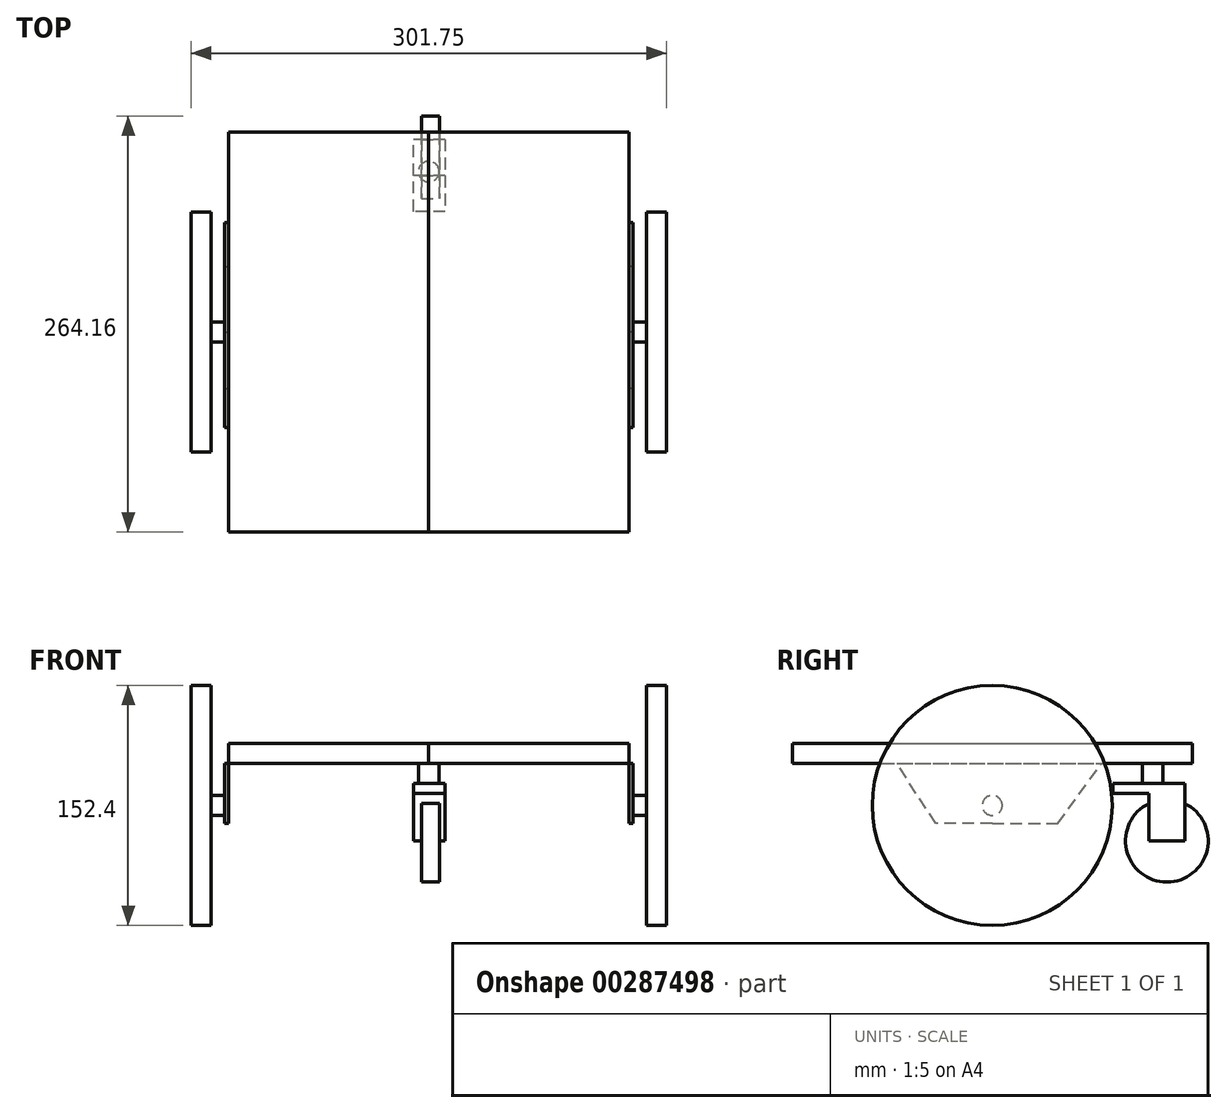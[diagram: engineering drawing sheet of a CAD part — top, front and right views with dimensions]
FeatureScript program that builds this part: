
annotation { "Feature Type Name" : "Feature", "Feature Type Description" : "" }
export const myFeature = defineFeature(function(context is Context, id is Id, definition is map)
    precondition{}
    {
        {
            var Q0;
            Q0=qCreatedBy(makeId("Top.planeOp"),FACE);
            var sketch = newSketch(context, id + "F0", { "sketchPlane" : qUnion([Q0])});
            skLineSegment(sketch, "E0.bottom", {"start": v(-82.1, -91.16) * mm, "end": v(44.9, -91.16) * mm});
            skLineSegment(sketch, "E0.top", {"start": v(-82.1, 162.84) * mm, "end": v(44.9, 162.84) * mm});
            skLineSegment(sketch, "E0.left", {"start": v(-82.1, -91.16) * mm, "end": v(-82.1, 162.84) * mm});
            skLineSegment(sketch, "E0.right", {"start": v(44.9, -91.16) * mm, "end": v(44.9, 162.84) * mm});
            skSolve(sketch);
        }
        {
            var Q0;
            Q0 = qSketchRegion(id + "F0", true);
            extrude(context, id + "F1", {"entities" : qUnion([Q0]), "depth" : 12.7 * mm});
        }
        {
            var Q0;
            Q0=makeQuery(id+"F1.opExtrude","SWEPT_FACE",FACE,{"disambiguationData":[OSD([sQuery(id+"F0.wireOp",EDGE,"E0.left")])]});
            var sketch = newSketch(context, id + "F2", { "sketchPlane" : qUnion([Q0])});
            skLineSegment(sketch, "E1", {"start": v(-35.84, 12.7) * mm, "end": v(-35.84, 0) * mm});
            skLineSegment(sketch, "E2", {"start": v(-35.84, 0) * mm, "end": v(-35.84, -26.62) * mm});
            skCircle(sketch, "E3", {"center": v(-35.84, -26.62) * mm, "radius": 6.35 * mm});
            skSolve(sketch);
        }
        {
            var Q0;
            Q0 = qSketchRegion(id + "F2", true);
            extrude(context, id + "F3", {"entities" : qUnion([Q0]), "depth" : 11.18 * mm});
        }
        {
            var Q0;
            Q0=makeQuery(id+"F3.opExtrude","CAP_FACE",FACE,{"disambiguationData":[OSD([sQuery(id+"F2.wireOp",EDGE,"E3")])],"isStart":false});
            var sketch = newSketch(context, id + "F4", { "sketchPlane" : qUnion([Q0])});
            skCircle(sketch, "E4", {"center": v(-35.84, -26.62) * mm, "radius": 76.2 * mm});
            skSolve(sketch);
        }
        {
            var Q0;
            Q0 = qSketchRegion(id + "F4", true);
            extrude(context, id + "F5", {"entities" : qUnion([Q0]), "operationType" : NewBodyOperationType.ADD, "depth" : 12.7 * mm});
        }
        {
            var Q0;
            Q0=makeQuery(id+"F1.opExtrude","SWEPT_FACE",FACE,{"disambiguationData":[OSD([sQuery(id+"F0.wireOp",EDGE,"E0.left")])]});
            var sketch = newSketch(context, id + "F6", { "sketchPlane" : qUnion([Q0])});
            skLineSegment(sketch, "E5.bottom", {"start": v(-35.84, 0) * mm, "end": v(0, 0) * mm});
            skLineSegment(sketch, "E5.top", {"start": v(-35.84, -38.12) * mm, "end": v(0, -38.12) * mm});
            skLineSegment(sketch, "E5.left", {"start": v(-35.84, 0) * mm, "end": v(-35.84, -38.12) * mm});
            skLineSegment(sketch, "E6.bottom", {"start": v(-35.84, 0) * mm, "end": v(-77.43, 0) * mm});
            skLineSegment(sketch, "E6.top", {"start": v(-35.84, -38.06) * mm, "end": v(-77.43, -38.06) * mm});
            skLineSegment(sketch, "E7", {"start": v(0, -38.12) * mm, "end": v(24.77, 0) * mm});
            skLineSegment(sketch, "E8", {"start": v(-77.43, -38.06) * mm, "end": v(-105.3, 0) * mm});
            skLineSegment(sketch, "E9", {"start": v(24.77, 0) * mm, "end": v(-105.3, 0) * mm});
            skSolve(sketch);
        }
        {
            var Q0;
            Q0 = qSketchRegion(id + "F6", true);
            extrude(context, id + "F7", {"entities" : qUnion([Q0]), "operationType" : NewBodyOperationType.ADD, "depth" : 2.54 * mm});
        }
        {
            var Q0;
            Q0=makeQuery(id+"F5.opExtrude","CAP_FACE",FACE,{"disambiguationData":[OSD([sQuery(id+"F4.wireOp",EDGE,"E4")])],"isStart":true});
            var sketch = newSketch(context, id + "F8", { "sketchPlane" : qUnion([Q0])});
            skCircle(sketch, "E10", {"center": v(35.84, -26.62) * mm, "radius": 19.05 * mm});
            skSolve(sketch);
        }
        {
            var Q0;
            Q0 = qSketchRegion(id + "F8", true);
            var Q1;
            Q1=sQuery(id+"F8.wireOp",EDGE,"E10");
            extrude(context, id + "F9", {"entities" : qUnion([Q0]), "bodyType" : ToolBodyType.SURFACE, "surfaceEntities" : qUnion([Q1]), "depth" : 70.36 * mm, "hasSecondDirection" : true, "secondDirectionOppositeDirection" : false, "secondDirectionDepth" : 10.92 * mm});
        }
        {
            var Q0;
            Q0=makeQuery(id+"F1.opExtrude","SWEPT_FACE",FACE,{"disambiguationData":[OSD([sQuery(id+"F0.wireOp",EDGE,"E0.right")])]});
            var sketch = newSketch(context, id + "F10", { "sketchPlane" : qUnion([Q0])});
            skLineSegment(sketch, "E11.bottom", {"start": v(-95.2, 36.48) * mm, "end": v(174.85, 36.48) * mm});
            skLineSegment(sketch, "E11.top", {"start": v(-95.2, -51.46) * mm, "end": v(174.85, -51.46) * mm});
            skLineSegment(sketch, "E11.left", {"start": v(-95.2, 36.48) * mm, "end": v(-95.2, -51.46) * mm});
            skLineSegment(sketch, "E11.right", {"start": v(174.85, 36.48) * mm, "end": v(174.85, -51.46) * mm});
            skSolve(sketch);
        }
        {
            var Q0;
            Q0=makeQuery(id+"F3.opExtrude","SWEPT_BODY",BODY,{"disambiguationData":[OSD([sQuery(id+"F2.wireOp",EDGE,"E3")])]});
            var Q1;
            Q1=makeQuery(id+"F1.opExtrude","SWEPT_BODY",BODY,{"disambiguationData":[OSD([sQuery(id+"F0.wireOp",EDGE,"E0.bottom"),sQuery(id+"F0.wireOp",EDGE,"E0.top"),sQuery(id+"F0.wireOp",EDGE,"E0.left"),sQuery(id+"F0.wireOp",EDGE,"E0.right")])]});
            var Q2;
            Q2=makeQuery(id+"F9.opExtrude","SWEPT_BODY",BODY,{"disambiguationData":[OSD([sQuery(id+"F8.wireOp",EDGE,"E10")])]});
            var Q3;
            Q3=makeQuery(id+"F10.imprint","IMPRINT",FACE,{"disambiguationData":[TD([[makeQuery(id+"F10.imprint","IMPRINT",EDGE,{"derivedFrom":sQuery(id+"F10.wireOp",EDGE,"E11.bottom")}),-1.0]])]});
            mirror(context, id + "F11", {"entities" : qUnion([Q0, Q1, Q2]), "mirrorPlane" : qUnion([Q3])});
        }
        {
            var Q0;
            Q0=makeQuery(id+"F11.opPattern","COPY",FACE,{"derivedFrom":makeQuery(id+"F1.opExtrude","CAP_FACE",FACE,{"disambiguationData":[OSD([sQuery(id+"F0.wireOp",EDGE,"E0.bottom"),sQuery(id+"F0.wireOp",EDGE,"E0.top"),sQuery(id+"F0.wireOp",EDGE,"E0.left"),sQuery(id+"F0.wireOp",EDGE,"E0.right")])],"isStart":true}),"instanceName":"1"});
            var sketch = newSketch(context, id + "F12", { "sketchPlane" : qUnion([Q0])});
            skCircle(sketch, "E12", {"center": v(44.9, -137.77) * mm, "radius": 6.56 * mm});
            skPoint(sketch, "E13.bottom.start.orphan", {"position": v(108.4, -162.84) * mm});
            skSolve(sketch);
        }
        {
            var Q0;
            Q0 = qSketchRegion(id + "F12", true);
            extrude(context, id + "F13", {"entities" : qUnion([Q0]), "depth" : 12.7 * mm});
        }
        {
            var Q0;
            Q0=makeQuery(id+"F13.opExtrude","CAP_FACE",FACE,{"disambiguationData":[OSD([sQuery(id+"F12.wireOp",EDGE,"E12")])],"isStart":false});
            var sketch = newSketch(context, id + "F14", { "sketchPlane" : qUnion([Q0])});
            skLineSegment(sketch, "E14", {"start": v(35.08, -112.45) * mm, "end": v(35.08, -158.17) * mm});
            skLineSegment(sketch, "E15", {"start": v(55.4, -158.17) * mm, "end": v(55.4, -112.45) * mm});
            skPoint(sketch, "E16.start.orphan", {"position": v(44.9, -137.77) * mm});
            skLineSegment(sketch, "E17", {"start": v(55.4, -158.17) * mm, "end": v(35.08, -158.17) * mm});
            skLineSegment(sketch, "E18", {"start": v(55.4, -112.45) * mm, "end": v(35.08, -112.45) * mm});
            skSolve(sketch);
        }
        {
            var Q0;
            Q0 = qSketchRegion(id + "F14", true);
            extrude(context, id + "F15", {"entities" : qUnion([Q0]), "operationType" : NewBodyOperationType.ADD, "depth" : 6.35 * mm});
        }
        {
            var Q0;
            Q0=makeQuery(id+"F15.opExtrude","CAP_FACE",FACE,{"disambiguationData":[OSD([sQuery(id+"F14.wireOp",EDGE,"MZ0X6NA9-6Hzz-H7Bn-aXP2-zpWHlnaENPtg"),sQuery(id+"F14.wireOp",EDGE,"E14"),sQuery(id+"F14.wireOp",EDGE,"ylwb5r81-WtZM-RIVS-pKZT-0xD2LLOTBBSw"),sQuery(id+"F14.wireOp",EDGE,"yOIh4wNm-CNTl-au8W-9sHh-K9dIQWkri87r"),sQuery(id+"F14.wireOp",EDGE,"E15"),sQuery(id+"F14.wireOp",EDGE,"3iRgoU3g-5YqV-YFtJ-8wj1-G1n6zFx17Cjh")])],"isStart":false});
            var sketch = newSketch(context, id + "F16", { "sketchPlane" : qUnion([Q0])});
            skLineSegment(sketch, "E19.bottom", {"start": v(55.4, -158.17) * mm, "end": v(35.08, -158.17) * mm});
            skLineSegment(sketch, "E19.top", {"start": v(55.4, -135.31) * mm, "end": v(35.08, -135.31) * mm});
            skLineSegment(sketch, "E19.left", {"start": v(55.4, -158.17) * mm, "end": v(55.4, -135.31) * mm});
            skLineSegment(sketch, "E19.right", {"start": v(35.08, -158.17) * mm, "end": v(35.08, -135.31) * mm});
            skSolve(sketch);
        }
        {
            var Q0;
            Q0=makeQuery(id+"F16.imprint","IMPRINT",FACE,{"disambiguationData":[TD([[makeQuery(id+"F16.imprint","IMPRINT",EDGE,{"derivedFrom":sQuery(id+"F16.wireOp",EDGE,"E19.bottom")}),-1.0]])]});
            extrude(context, id + "F17", {"entities" : qUnion([Q0]), "operationType" : NewBodyOperationType.ADD, "depth" : 29.97 * mm});
        }
        {
            var Q0;
            Q0=makeQuery(id+"F17.boolean.opBoolean","MERGE",FACE,{"derivedFrom":[makeQuery(id+"F15.opExtrude","SWEPT_FACE",FACE,{"disambiguationData":[OSD([sQuery(id+"F14.wireOp",EDGE,"E15")])]}),makeQuery(id+"F17.opExtrude","SWEPT_FACE",FACE,{"disambiguationData":[OSD([sQuery(id+"F16.wireOp",EDGE,"E19.left")])]})]});
            var sketch = newSketch(context, id + "F18", { "sketchPlane" : qUnion([Q0])});
            skCircle(sketch, "E20", {"center": v(146.74, -49.02) * mm, "radius": 26.26 * mm});
            skSolve(sketch);
        }
        {
            var Q0;
            Q0 = qSketchRegion(id + "F18", true);
            extrude(context, id + "F19", {"entities" : qUnion([Q0]), "operationType" : NewBodyOperationType.ADD, "oppositeDirection" : true, "depth" : 15.24 * mm, "hasSecondDirection" : true, "secondDirectionOppositeDirection" : true, "secondDirectionDepth" : 3.8 * mm});
        }
    });
